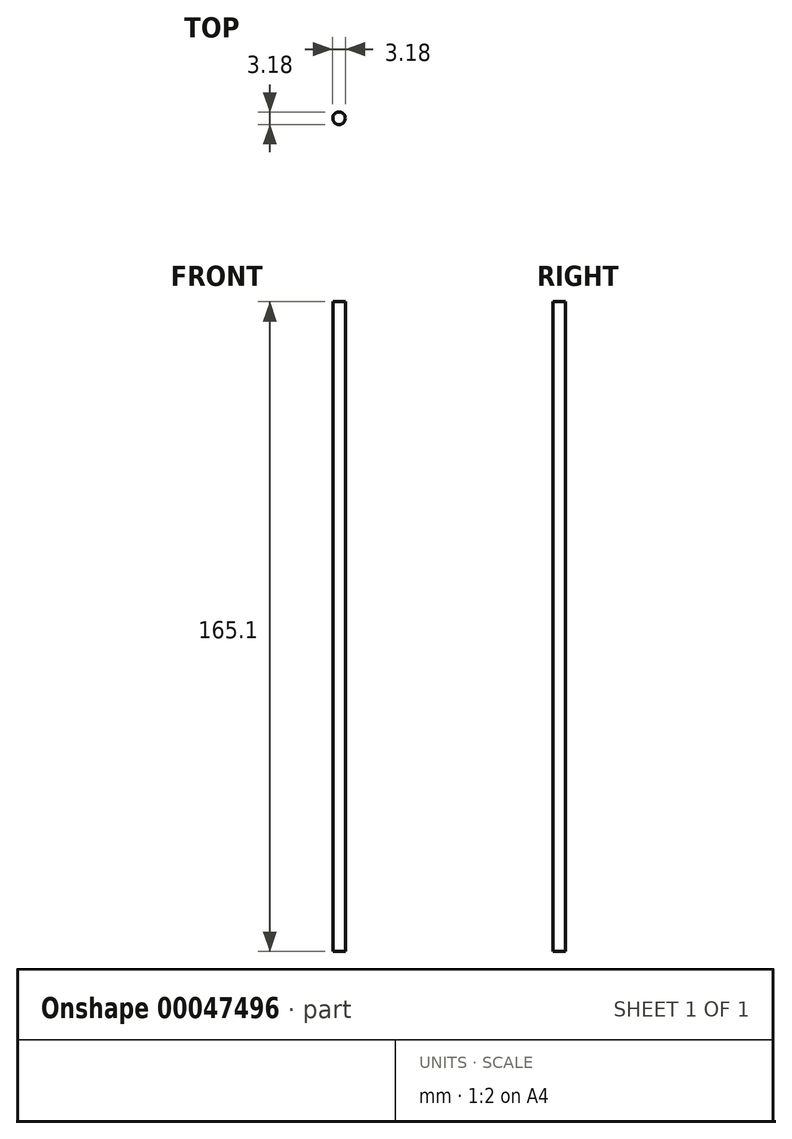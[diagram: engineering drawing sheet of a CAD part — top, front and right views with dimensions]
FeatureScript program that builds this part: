
annotation { "Feature Type Name" : "Feature", "Feature Type Description" : "" }
export const myFeature = defineFeature(function(context is Context, id is Id, definition is map)
    precondition{}
    {
        {
            var Q0;
            Q0=qCreatedBy(makeId("Top.planeOp"),FACE);
            var sketch = newSketch(context, id + "F0", { "sketchPlane" : qUnion([Q0])});
            skCircle(sketch, "E0", {"center": v(0, 0) * mm, "radius": 1.59 * mm});
            skSolve(sketch);
        }
        {
            var Q0;
            Q0 = qSketchRegion(id + "F0", true);
            extrude(context, id + "F1", {"entities" : qUnion([Q0]), "depth" : 165.1 * mm, "symmetric" : true});
        }
    });
